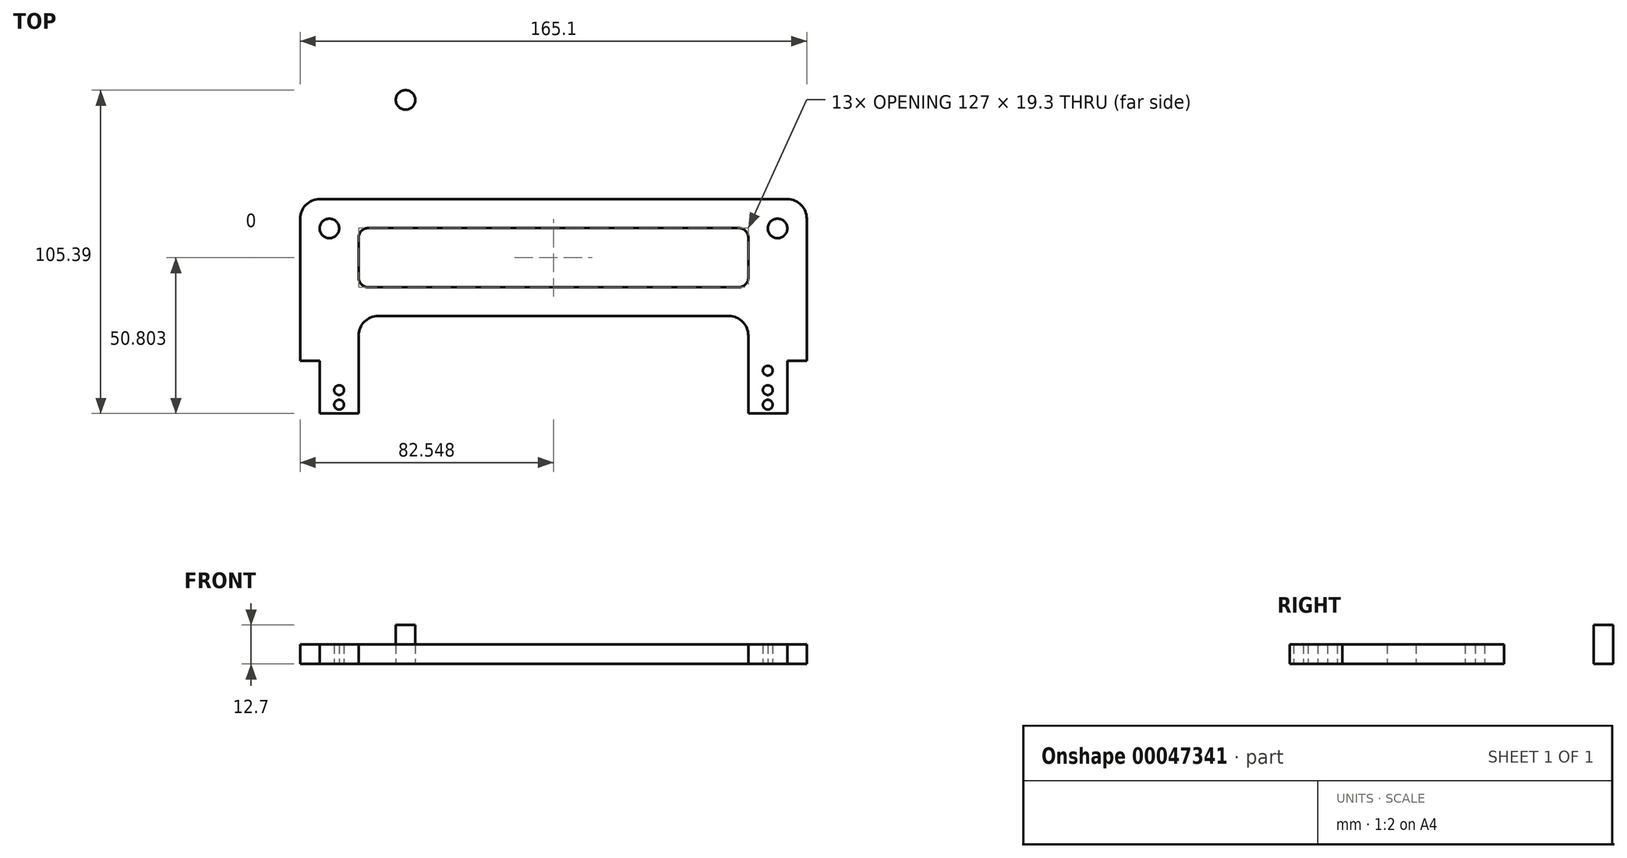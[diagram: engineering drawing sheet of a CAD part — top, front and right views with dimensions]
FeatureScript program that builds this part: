
annotation { "Feature Type Name" : "Feature", "Feature Type Description" : "" }
export const myFeature = defineFeature(function(context is Context, id is Id, definition is map)
    precondition{}
    {
        {
            var Q0;
            Q0=qCreatedBy(makeId("Top.planeOp"),FACE);
            var sketch = newSketch(context, id + "F0", { "sketchPlane" : qUnion([Q0])});
            skLineSegment(sketch, "E0", {"start": v(-73.83, -13.8) * mm, "end": v(-67.48, -13.8) * mm});
            skLineSegment(sketch, "E1", {"start": v(-67.48, -13.8) * mm, "end": v(-67.48, -30.95) * mm});
            skLineSegment(sketch, "E2", {"start": v(-67.48, -30.95) * mm, "end": v(-54.78, -30.95) * mm});
            skLineSegment(sketch, "E3", {"start": v(-54.78, -30.95) * mm, "end": v(-54.78, -5.55) * mm});
            skLineSegment(sketch, "E4", {"start": v(-48.43, 0.8) * mm, "end": v(65.87, 0.8) * mm});
            skLineSegment(sketch, "E5", {"start": v(72.22, -5.55) * mm, "end": v(72.22, -13.8) * mm});
            skLineSegment(sketch, "E6", {"start": v(72.22, -30.95) * mm, "end": v(84.92, -30.95) * mm});
            skLineSegment(sketch, "E7", {"start": v(84.92, -30.95) * mm, "end": v(84.92, -13.8) * mm});
            skLineSegment(sketch, "E8", {"start": v(84.92, -13.8) * mm, "end": v(91.27, -13.8) * mm});
            skLineSegment(sketch, "E9", {"start": v(91.27, -13.8) * mm, "end": v(91.27, 32.55) * mm});
            skLineSegment(sketch, "E10", {"start": v(84.92, 38.9) * mm, "end": v(8.72, 38.9) * mm});
            skLineSegment(sketch, "E11", {"start": v(-73.83, 32.55) * mm, "end": v(-73.83, -13.8) * mm});
            skLineSegment(sketch, "E12", {"start": v(-47.57, 0.8) * mm, "end": v(-47.57, 38.9) * mm, "construction": true});
            skLineSegment(sketch, "E13", {"start": v(72.22, -20.15) * mm, "end": v(78.57, -20.15) * mm, "construction": true});
            skLineSegment(sketch, "E14", {"start": v(78.57, -20.15) * mm, "end": v(78.57, -20.15) * mm});
            skLineSegment(sketch, "E15", {"start": v(78.57, -20.15) * mm, "end": v(84.92, -20.15) * mm, "construction": true});
            skCircle(sketch, "E16", {"center": v(78.57, -16.98) * mm, "radius": 1.59 * mm});
            skLineSegment(sketch, "E17.bottom", {"start": v(-51.6, 29.5) * mm, "end": v(69.04, 29.5) * mm});
            skLineSegment(sketch, "E17.top", {"start": v(-51.6, 10.2) * mm, "end": v(69.04, 10.2) * mm});
            skLineSegment(sketch, "E17.left", {"start": v(-54.78, 26.33) * mm, "end": v(-54.78, 13.38) * mm});
            skLineSegment(sketch, "E17.right", {"start": v(72.22, 26.33) * mm, "end": v(72.22, 13.38) * mm});
            skLineSegment(sketch, "E18", {"start": v(-30.66, 10.2) * mm, "end": v(-30.66, 0.8) * mm, "construction": true});
            skLineSegment(sketch, "E19", {"start": v(-31.04, 29.5) * mm, "end": v(-31.04, 38.9) * mm, "construction": true});
            skCircle(sketch, "E20", {"center": v(-64.3, 29.38) * mm, "radius": 3.18 * mm});
            skLineSegment(sketch, "E21", {"start": v(-64.3, 38.9) * mm, "end": v(-64.3, 32.55) * mm, "construction": true});
            skLineSegment(sketch, "E22", {"start": v(-73.83, 29.38) * mm, "end": v(-67.48, 29.38) * mm, "construction": true});
            skLineSegment(sketch, "E23", {"start": v(8.72, 38.9) * mm, "end": v(8.72, 67) * mm, "construction": true});
            skLineSegment(sketch, "E24", {"start": v(8.72, 38.9) * mm, "end": v(-67.48, 38.9) * mm});
            skCircle(sketch, "E25.MirrorC", {"center": v(81.74, 29.38) * mm, "radius": 3.18 * mm});
            skLineSegment(sketch, "E26", {"start": v(78.57, -23.33) * mm, "end": v(78.57, -26.5) * mm, "construction": true});
            skCircle(sketch, "E27", {"center": v(78.57, -23.33) * mm, "radius": 1.59 * mm});
            skCircle(sketch, "E28.MirrorC", {"center": v(-61.13, -23.33) * mm, "radius": 1.59 * mm});
            skLineSegment(sketch, "E29", {"start": v(78.57, -20.15) * mm, "end": v(78.57, -23.33) * mm, "construction": true});
            skLineSegment(sketch, "E30", {"start": v(84.92, -13.8) * mm, "end": v(72.22, -13.8) * mm, "construction": true});
            skLineSegment(sketch, "E31", {"start": v(78.57, -16.98) * mm, "end": v(78.57, -13.8) * mm, "construction": true});
            skLineSegment(sketch, "E32", {"start": v(78.57, -16.98) * mm, "end": v(78.57, -20.15) * mm, "construction": true});
            skLineSegment(sketch, "E33", {"start": v(72.22, -20.15) * mm, "end": v(72.22, -30.95) * mm});
            skLineSegment(sketch, "E34", {"start": v(72.22, -13.8) * mm, "end": v(72.22, -20.15) * mm});
            skPoint(sketch, "E35.visualSharp", {"position": v(91.27, 38.9) * mm});
            skArc(sketch, "E35.filletArc", {"start": v(91.27, 32.55) * mm, "mid": v(89.4, 37.04) * mm, "end": v(84.92, 38.9) * mm});
            skPoint(sketch, "E36.visualSharp", {"position": v(-73.83, 38.9) * mm});
            skArc(sketch, "E36.filletArc", {"start": v(-67.48, 38.9) * mm, "mid": v(-71.97, 37.04) * mm, "end": v(-73.83, 32.55) * mm});
            skPoint(sketch, "E37.visualSharp", {"position": v(-54.78, 0.8) * mm});
            skArc(sketch, "E37.filletArc", {"start": v(-48.43, 0.8) * mm, "mid": v(-52.92, -1.06) * mm, "end": v(-54.78, -5.55) * mm});
            skPoint(sketch, "E38.visualSharp", {"position": v(72.22, 0.8) * mm});
            skArc(sketch, "E38.filletArc", {"start": v(72.22, -5.55) * mm, "mid": v(70.36, -1.06) * mm, "end": v(65.87, 0.8) * mm});
            skLineSegment(sketch, "E39", {"start": v(78.57, -28.09) * mm, "end": v(78.57, -30.95) * mm, "construction": true});
            skCircle(sketch, "E40", {"center": v(78.57, -28.09) * mm, "radius": 1.59 * mm});
            skLineSegment(sketch, "E41", {"start": v(78.57, -26.5) * mm, "end": v(78.57, -28.09) * mm, "construction": true});
            skLineSegment(sketch, "E42", {"start": v(78.57, -26.5) * mm, "end": v(72.22, -26.5) * mm, "construction": true});
            skLineSegment(sketch, "E43", {"start": v(78.57, -26.5) * mm, "end": v(84.92, -26.5) * mm, "construction": true});
            skLineSegment(sketch, "E44", {"start": v(75.4, -26.5) * mm, "end": v(75.4, -30.95) * mm, "construction": true});
            skCircle(sketch, "E45.MirrorC", {"center": v(-61.13, -28.09) * mm, "radius": 1.59 * mm});
            skPoint(sketch, "E46.visualSharp", {"position": v(-54.78, 10.2) * mm});
            skArc(sketch, "E46.filletArc", {"start": v(-54.78, 13.38) * mm, "mid": v(-53.85, 11.13) * mm, "end": v(-51.6, 10.2) * mm});
            skPoint(sketch, "E47.visualSharp", {"position": v(-54.78, 29.5) * mm});
            skArc(sketch, "E47.filletArc", {"start": v(-51.6, 29.5) * mm, "mid": v(-53.85, 28.58) * mm, "end": v(-54.78, 26.33) * mm});
            skPoint(sketch, "E48.visualSharp", {"position": v(72.22, 29.5) * mm});
            skArc(sketch, "E48.filletArc", {"start": v(72.22, 26.33) * mm, "mid": v(71.29, 28.58) * mm, "end": v(69.04, 29.5) * mm});
            skPoint(sketch, "E49.visualSharp", {"position": v(72.22, 10.2) * mm});
            skArc(sketch, "E49.filletArc", {"start": v(69.04, 10.2) * mm, "mid": v(71.29, 11.13) * mm, "end": v(72.22, 13.38) * mm});
            skSolve(sketch);
        }
        {
            var Q0;
            Q0 = qSketchRegion(id + "F0", true);
            extrude(context, id + "F1", {"entities" : qUnion([Q0]), "depth" : 6.35 * mm});
        }
        {
            var Q0;
            Q0=qCreatedBy(makeId("Top.planeOp"),FACE);
            var sketch = newSketch(context, id + "F2", { "sketchPlane" : qUnion([Q0])});
            skCircle(sketch, "E50", {"center": v(-39.48, 71.26) * mm, "radius": 3.17 * mm});
            skSolve(sketch);
        }
        {
            var Q0;
            Q0 = qSketchRegion(id + "F2", true);
            extrude(context, id + "F3", {"entities" : qUnion([Q0]), "depth" : 12.7 * mm});
        }
    });
